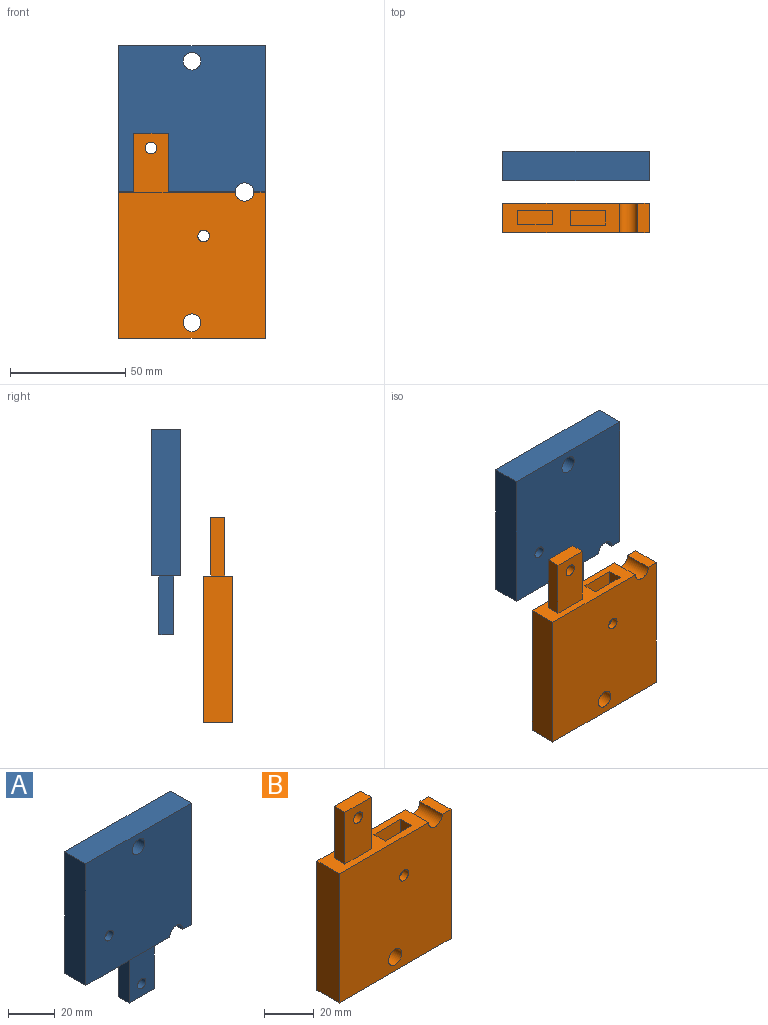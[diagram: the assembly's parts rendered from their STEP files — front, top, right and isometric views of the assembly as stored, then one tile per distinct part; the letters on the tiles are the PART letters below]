
ASSEMBLY  parts=2 mates=1
PART A: 22 faces, bbox 63.5x12.7x88.9 mm
  f0: plane 50.56x12.7mm, normal (0,0,-1), area 448.6mm2, adj f4,f5,f6,f7,f9,f10,f11,f12
  f1: plane 12.7x5mm, normal (0,0,-1), area 63.5mm2, adj f2,f5,f6,f7
  f2: plane 63.5x12.7mm, normal (1,0,0), area 806.5mm2, adj f1,f3,f5,f6
  f3: plane 63.5x12.7mm, normal (0,0,1), area 806.5mm2, adj f2,f4,f5,f6
  f4: plane 63.5x12.7mm, normal (-1,0,0), area 806.5mm2, adj f0,f3,f5,f6
  f5: plane 63.5x63.5mm, normal (0,-1,0), area 3941.6mm2, adj f0,f1,f2,f3,f4,f7,f8,f21
  f6: plane 63.5x63.5mm, normal (0,1,0), area 3941.6mm2, adj f0,f1,f2,f3,f4,f7,f8,f20
  f7: cylinder r=3.97mm len=12.7mm, axis (0,-1,0), area 158.3mm2, adj f0,f1,f5,f6
  f8: cylinder r=3.81mm len=12.7mm, axis (0,-1,0), area 304mm2, adj f5,f6
  f9: plane 25.4x6.35mm, normal (1,0,0), area 161.3mm2, adj f0,f10,f12,f13
  f10: plane 25.4x15.24mm, normal (0,-1,0), area 366.8mm2, adj f0,f9,f11,f13,f19
  f11: plane 25.4x6.35mm, normal (-1,0,0), area 161.3mm2, adj f0,f10,f12,f13
  f12: plane 25.4x15.24mm, normal (0,1,0), area 366.8mm2, adj f0,f9,f11,f13,f19
  f13: plane 15.24x6.35mm, normal (0,0,-1), area 96.8mm2, adj f9,f10,f11,f12
  f14: plane 25.4x6.35mm, normal (-1,0,0), area 161.3mm2, adj f0,f15,f17,f18
  f15: plane 25.4x15.24mm, normal (0,1,0), area 366.8mm2, adj f0,f14,f16,f18,f21
  f16: plane 25.4x6.35mm, normal (1,0,0), area 161.3mm2, adj f0,f15,f17,f18
  f17: plane 25.4x15.24mm, normal (0,-1,0), area 366.8mm2, adj f0,f14,f16,f18,f20
  f18: plane 15.24x6.35mm, normal (0,0,-1), area 96.8mm2, adj f14,f15,f16,f17
  f19: cylinder r=2.54mm len=6.35mm, axis (0,-1,0), area 101.3mm2, adj f10,f12
  f20: cylinder r=2.54mm len=5.08mm, axis (0,-1,0), area 50.7mm2, adj f6,f17
  f21: cylinder r=2.54mm len=5.08mm, axis (0,-1,0), area 50.7mm2, adj f5,f15
PART B: 22 faces, bbox 63.5x12.7x88.9 mm
  f0: plane 50.56x12.7mm, normal (0,0,1), area 454mm2, adj f3,f5,f6,f7,f8,f9,f10,f11
  f1: plane 12.7x5mm, normal (0,0,1), area 63.5mm2, adj f2,f5,f6,f7
  f2: plane 63.5x12.7mm, normal (1,0,0), area 806.5mm2, adj f1,f4,f5,f6
  f3: plane 63.5x12.7mm, normal (-1,0,0), area 806.5mm2, adj f0,f4,f5,f6
  f4: plane 63.5x12.7mm, normal (0,0,-1), area 806.5mm2, adj f2,f3,f5,f6
  f5: plane 63.5x63.5mm, normal (0,-1,0), area 3941.6mm2, adj f0,f1,f2,f3,f4,f7,f19,f21
  f6: plane 63.5x63.5mm, normal (0,1,0), area 3941.6mm2, adj f0,f1,f2,f3,f4,f7,f20,f21
  f7: cylinder r=3.97mm len=12.7mm, axis (0,-1,0), area 158.3mm2, adj f0,f1,f5,f6
  f8: plane 25.4x6.1mm, normal (1,0,0), area 154.8mm2, adj f0,f9,f11,f12
  f9: plane 25.4x14.99mm, normal (0,1,0), area 360.4mm2, adj f0,f8,f10,f12,f13
  f10: plane 25.4x6.1mm, normal (-1,0,0), area 154.8mm2, adj f0,f9,f11,f12
  f11: plane 25.4x14.99mm, normal (0,-1,0), area 360.4mm2, adj f0,f8,f10,f12,f13
  f12: plane 14.99x6.1mm, normal (0,0,1), area 91.4mm2, adj f8,f9,f10,f11
  f13: cylinder r=2.54mm len=6.1mm, axis (0,-1,0), area 97.3mm2, adj f9,f11
  f14: plane 25.4x6.35mm, normal (-1,0,0), area 161.3mm2, adj f0,f15,f17,f18
  f15: plane 25.4x15.24mm, normal (0,-1,0), area 366.8mm2, adj f0,f14,f16,f18,f20
  f16: plane 25.4x6.35mm, normal (1,0,0), area 161.3mm2, adj f0,f15,f17,f18
  f17: plane 25.4x15.24mm, normal (0,1,0), area 366.8mm2, adj f0,f14,f16,f18,f19
  f18: plane 15.24x6.35mm, normal (0,0,1), area 96.8mm2, adj f14,f15,f16,f17
  f19: cylinder r=2.54mm len=5.08mm, axis (0,-1,0), area 50.7mm2, adj f5,f17
  f20: cylinder r=2.54mm len=5.08mm, axis (0,-1,0), area 50.7mm2, adj f6,f15
  f21: cylinder r=3.81mm len=12.7mm, axis (0,-1,0), area 304mm2, adj f5,f6
PLACE A t=(46.43,59.02,57.53)mm
PLACE B t=(46.43,36.65,-5.97)mm
MATE cylindrical B.f13 <-> A.f20  axis (0,-1,0) through (28.65,36.65,44.83)mm
